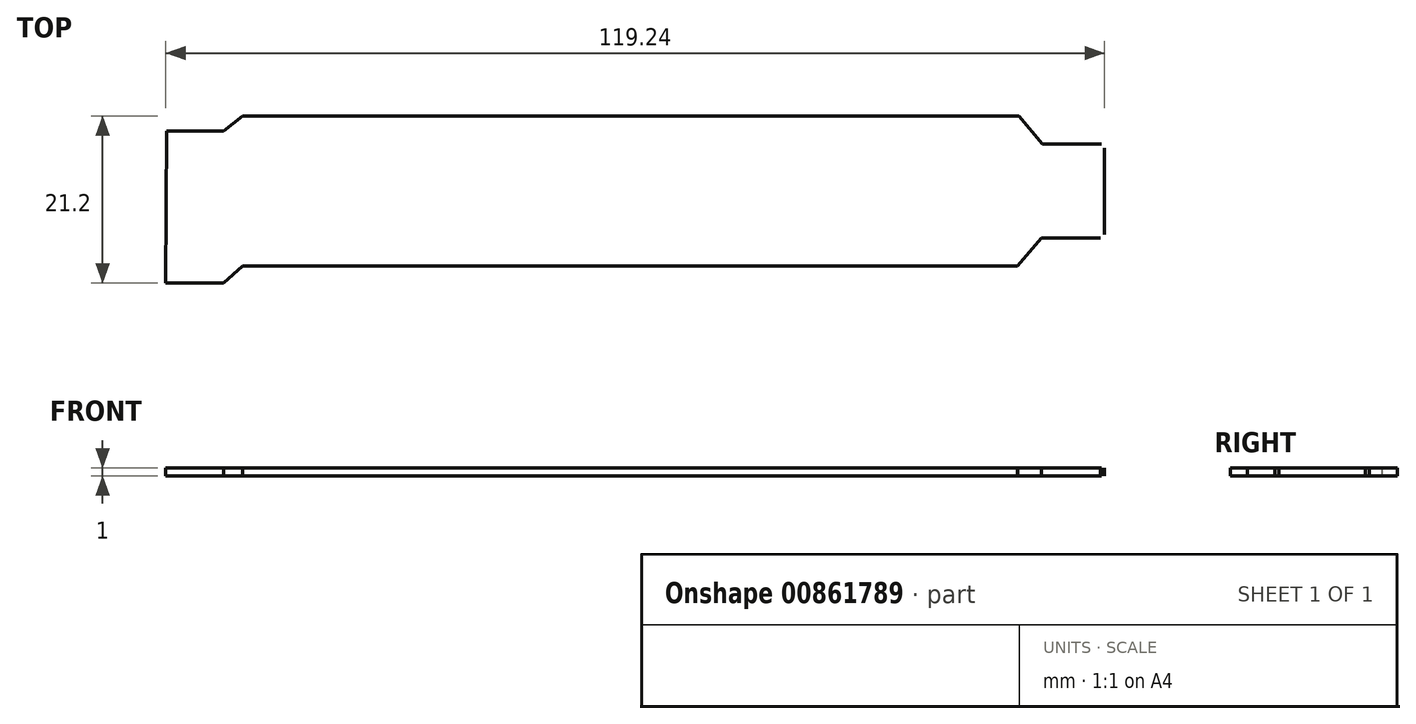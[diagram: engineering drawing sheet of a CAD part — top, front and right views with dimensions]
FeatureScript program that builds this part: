
annotation { "Feature Type Name" : "Feature", "Feature Type Description" : "" }
export const myFeature = defineFeature(function(context is Context, id is Id, definition is map)
    precondition{}
    {
        {
            var Q0;
            Q0=qCreatedBy(makeId("Top.planeOp"),FACE);
            var sketch = newSketch(context, id + "F0", { "sketchPlane" : qUnion([Q0])});
            skLineSegment(sketch, "E0", {"start": v(-58.87, 8.63) * mm, "end": v(-51.62, 8.63) * mm});
            skLineSegment(sketch, "E1", {"start": v(-51.62, 8.63) * mm, "end": v(-49.17, 10.52) * mm});
            skLineSegment(sketch, "E2", {"start": v(-49.17, 10.52) * mm, "end": v(49.39, 10.52) * mm});
            skLineSegment(sketch, "E3", {"start": v(49.39, 10.52) * mm, "end": v(52.4, 6.96) * mm});
            skLineSegment(sketch, "E4", {"start": v(52.4, 6.96) * mm, "end": v(59.87, 6.96) * mm});
            skLineSegment(sketch, "E5", {"start": v(59.87, 6.96) * mm, "end": v(60.27, 6.46) * mm});
            skLineSegment(sketch, "E6", {"start": v(60.27, 6.46) * mm, "end": v(60.27, -4.5) * mm});
            skLineSegment(sketch, "E7", {"start": v(60.27, -4.5) * mm, "end": v(59.77, -5) * mm});
            skLineSegment(sketch, "E8", {"start": v(59.77, -5) * mm, "end": v(52.27, -5) * mm});
            skLineSegment(sketch, "E9", {"start": v(52.27, -5) * mm, "end": v(49.25, -8.5) * mm});
            skLineSegment(sketch, "E10", {"start": v(49.25, -8.5) * mm, "end": v(-49.17, -8.5) * mm});
            skLineSegment(sketch, "E11", {"start": v(-49.17, -8.5) * mm, "end": v(-51.62, -10.68) * mm});
            skLineSegment(sketch, "E12", {"start": v(-51.62, -10.68) * mm, "end": v(-58.97, -10.68) * mm});
            skLineSegment(sketch, "E13", {"start": v(-58.97, -10.68) * mm, "end": v(-58.87, 8.63) * mm});
            skSolve(sketch);
        }
        {
            var Q0;
            Q0=makeQuery(id+"F0.imprint","IMPRINT",FACE,{"disambiguationData":[TD([[makeQuery(id+"F0.imprint","IMPRINT",EDGE,{"derivedFrom":sQuery(id+"F0.wireOp",EDGE,"E0")}),-1.0]])]});
            var Q1;
            Q1=sQuery(id+"F0.wireOp",EDGE,"E2");
            var Q2;
            Q2=sQuery(id+"F0.wireOp",EDGE,"E11");
            var Q3;
            Q3=sQuery(id+"F0.wireOp",EDGE,"E12");
            var Q4;
            Q4=sQuery(id+"F0.wireOp",EDGE,"E13");
            var Q5;
            Q5=sQuery(id+"F0.wireOp",EDGE,"E0");
            var Q6;
            Q6=sQuery(id+"F0.wireOp",EDGE,"E1");
            var Q7;
            Q7=sQuery(id+"F0.wireOp",EDGE,"E3");
            var Q8;
            Q8=sQuery(id+"F0.wireOp",EDGE,"E4");
            var Q9;
            Q9=sQuery(id+"F0.wireOp",EDGE,"E6");
            var Q10;
            Q10=sQuery(id+"F0.wireOp",EDGE,"E8");
            var Q11;
            Q11=sQuery(id+"F0.wireOp",EDGE,"E9");
            var Q12;
            Q12=sQuery(id+"F0.wireOp",EDGE,"E10");
            extrude(context, id + "F1", {"entities" : qUnion([Q0]), "bodyType" : ToolBodyType.SURFACE, "surfaceEntities" : qUnion([Q1, Q2, Q3, Q4, Q5, Q6, Q7, Q8, Q9, Q10, Q11, Q12]), "depth" : 1 * mm, "offsetDistance" : 25 * mm});
        }
    });
